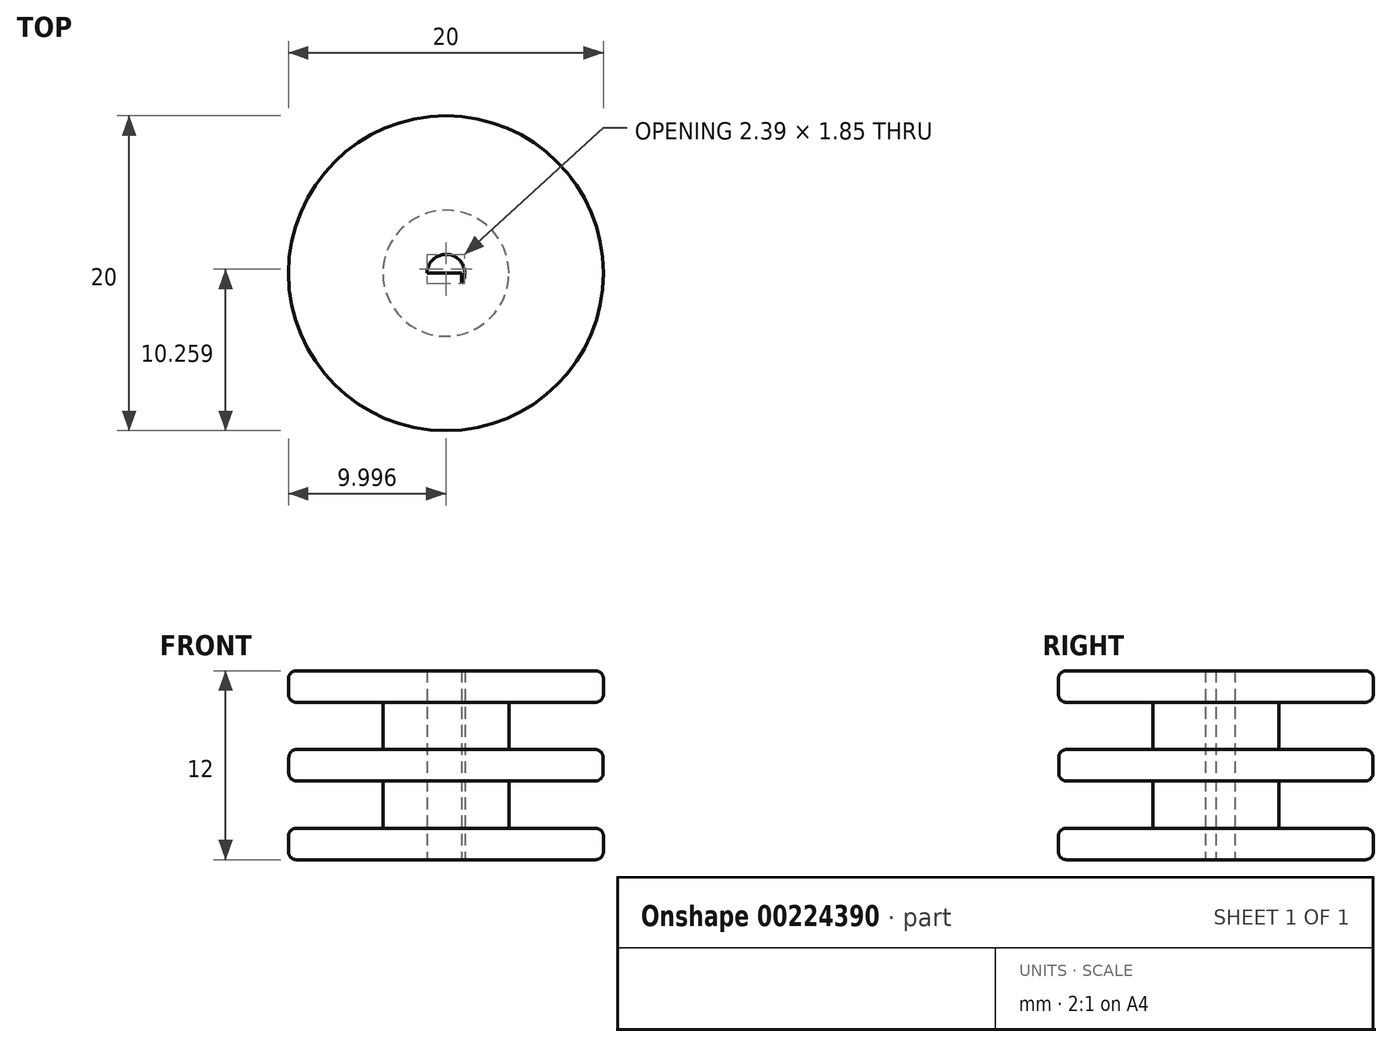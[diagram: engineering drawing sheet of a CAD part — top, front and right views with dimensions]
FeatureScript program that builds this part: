
annotation { "Feature Type Name" : "Feature", "Feature Type Description" : "" }
export const myFeature = defineFeature(function(context is Context, id is Id, definition is map)
    precondition{}
    {
        {
            var Q0;
            Q0=qCreatedBy(makeId("Top.planeOp"),FACE);
            var sketch = newSketch(context, id + "F0", { "sketchPlane" : qUnion([Q0])});
            skCircle(sketch, "E0", {"center": v(0, 0) * mm, "radius": 10 * mm});
            skCircle(sketch, "E1", {"center": v(0, 0) * mm, "radius": 4 * mm});
            skCircle(sketch, "E2", {"center": v(0, 0) * mm, "radius": 1.2 * mm});
            skLineSegment(sketch, "E3", {"start": v(-1.2, 0) * mm, "end": v(1, 0) * mm});
            skLineSegment(sketch, "E4", {"start": v(1, 0) * mm, "end": v(1, 0.66) * mm});
            skLineSegment(sketch, "E5", {"start": v(1, 0.66) * mm, "end": v(1, -0.66) * mm});
            skSolve(sketch);
        }
        {
            var Q0;
            Q0=makeQuery(id+"F0.imprint","IMPRINT",FACE,{"disambiguationData":[TD([[makeQuery(id+"F0.imprint","IMPRINT",EDGE,{"derivedFrom":sQuery(id+"F0.wireOp",EDGE,"E0")}),1.0]])]});
            extrude(context, id + "F1", {"entities" : qUnion([Q0]), "depth" : 2 * mm});
        }
        {
            var Q0;
            Q0=makeQuery(id+"F0.imprint","IMPRINT",FACE,{"disambiguationData":[TD([[makeQuery(id+"F0.imprint","IMPRINT",EDGE,{"derivedFrom":sQuery(id+"F0.wireOp",EDGE,"E1")}),1.0]])]});
            var Q1;
            {var subQ0=sQuery(id+"F0.wireOp",EDGE,"E5");var subQ1=sQuery(id+"F0.wireOp",EDGE,"E2");var subQ2=makeQuery(id+"F0.imprint","INTERSECT",VERTEX,{"disambiguationData":[OD(0.0)],"derivedFrom":[subQ1,subQ0]});Q1=makeQuery(id+"F0.imprint","IMPRINT",FACE,{"disambiguationData":[TD([[makeQuery(id+"F0.imprint","IMPRINT",EDGE,{"disambiguationData":[TD([[subQ2,1.0]])],"derivedFrom":subQ1}),1.0]])]});}
            extrude(context, id + "F2", {"entities" : qUnion([Q0, Q1]), "operationType" : NewBodyOperationType.ADD, "depth" : 6 * mm});
        }
        {
            var Q0;
            Q0=makeQuery(id+"F2.opExtrude","CAP_FACE",FACE,{"disambiguationData":[OSD([sQuery(id+"F0.wireOp",EDGE,"E1"),sQuery(id+"F0.wireOp",EDGE,"E2"),sQuery(id+"F0.wireOp",EDGE,"E5")])],"isStart":false});
            var sketch = newSketch(context, id + "F3", { "sketchPlane" : qUnion([Q0])});
            skCircle(sketch, "E6", {"center": v(0, 0) * mm, "radius": 9.98 * mm});
            skCircle(sketch, "E7", {"center": v(0, 0) * mm, "radius": 10 * mm});
            skSolve(sketch);
        }
        {
            var Q0;
            Q0=makeQuery(id+"F3.imprint","IMPRINT",FACE,{"disambiguationData":[TD([[makeQuery(id+"F3.imprint","IMPRINT",EDGE,{"derivedFrom":sQuery(id+"F3.wireOp",EDGE,"E6")}),1.0]])]});
            extrude(context, id + "F4", {"entities" : qUnion([Q0]), "operationType" : NewBodyOperationType.ADD, "oppositeDirection" : true, "depth" : 1 * mm});
        }
        {
            var Q0;
            Q0=qCreatedBy(makeId("Top.planeOp"),FACE);
            cPlane(context, id + "F5", {"entities" : qUnion([Q0]), "cplaneType" : CPlaneType.OFFSET, "offset" : 6 * mm, "width" : 150 * mm, "height" : 150 * mm});
        }
        {
            var Q0;
            Q0=makeQuery(id+"F1.opExtrude","SWEPT_BODY",BODY,{"disambiguationData":[OSD([sQuery(id+"F0.wireOp",EDGE,"E0"),sQuery(id+"F0.wireOp",EDGE,"E1")])]});
            var Q1;
            Q1=qCreatedBy(id+"F5.planeOp",FACE);
            mirror(context, id + "F6", {"operationType" : NewBodyOperationType.ADD, "entities" : qUnion([Q0]), "mirrorPlane" : qUnion([Q1])});
        }
        {
            var Q0;
            Q0=makeQuery(id+"F6.opPattern","COPY",EDGE,{"derivedFrom":makeQuery(id+"F4.opExtrude","CAP_EDGE",EDGE,{"disambiguationData":[OSD([sQuery(id+"F3.wireOp",EDGE,"E6")])],"isStart":false}),"instanceName":"1"});
            var Q1;
            Q1=makeQuery(id+"F4.opExtrude","CAP_EDGE",EDGE,{"disambiguationData":[OSD([sQuery(id+"F3.wireOp",EDGE,"E6")])],"isStart":false});
            var Q2;
            Q2=makeQuery(id+"F6.opPattern","COPY",EDGE,{"derivedFrom":makeQuery(id+"F1.opExtrude","CAP_EDGE",EDGE,{"disambiguationData":[OSD([sQuery(id+"F0.wireOp",EDGE,"E0")])],"isStart":false}),"instanceName":"1"});
            var Q3;
            Q3=makeQuery(id+"F1.opExtrude","CAP_EDGE",EDGE,{"disambiguationData":[OSD([sQuery(id+"F0.wireOp",EDGE,"E0")])],"isStart":false});
            var Q4;
            Q4=makeQuery(id+"F6.opPattern","COPY",EDGE,{"derivedFrom":makeQuery(id+"F1.opExtrude","CAP_EDGE",EDGE,{"disambiguationData":[OSD([sQuery(id+"F0.wireOp",EDGE,"E0")])],"isStart":true}),"instanceName":"1"});
            var Q5;
            Q5=makeQuery(id+"F1.opExtrude","CAP_EDGE",EDGE,{"disambiguationData":[OSD([sQuery(id+"F0.wireOp",EDGE,"E0")])],"isStart":true});
            fillet(context, id + "F7", {"entities" : qUnion([Q0, Q1, Q2, Q3, Q4, Q5]), "radius" : 0.5 * mm, "tangentPropagation" : true, "allowEdgeOverflow" : false});
        }
    });
